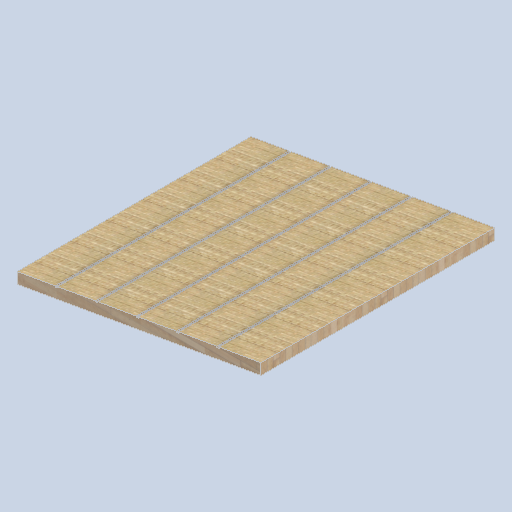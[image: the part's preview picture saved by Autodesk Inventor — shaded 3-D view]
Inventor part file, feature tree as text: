
AUTODESK INVENTOR PART (.ipt)
format: ipt  version: 2024.2 (Build 282272000, 272)  size: 253,440 bytes
history: native  units: in
note: dims shown in document units (in); Inventor stores cm internally (conversion verified against a paired STEP export)
features: sketch x4, other x3, plane x3
ambient origin geometry x8: Origin, YZ Plane, XZ Plane, XY Plane, X Axis, Y Axis, Z Axis, Center Point
bodies: Solid1 (feature_tree)
feature tree (10):
  other  "eave_panel_side.ipt"
  other  "Solid1::eave_panel_side.ipt"
  other  "TaggingFeature1"
  sketch  "Sketch1"  dims[d0=0.3937in]
  sketch  "Sketch2"
  sketch  "Sketch3"
  sketch  "Sketch4"
  plane  "Work Plane1"
  plane  "Work Plane2"
  plane  "Work Plane3"
